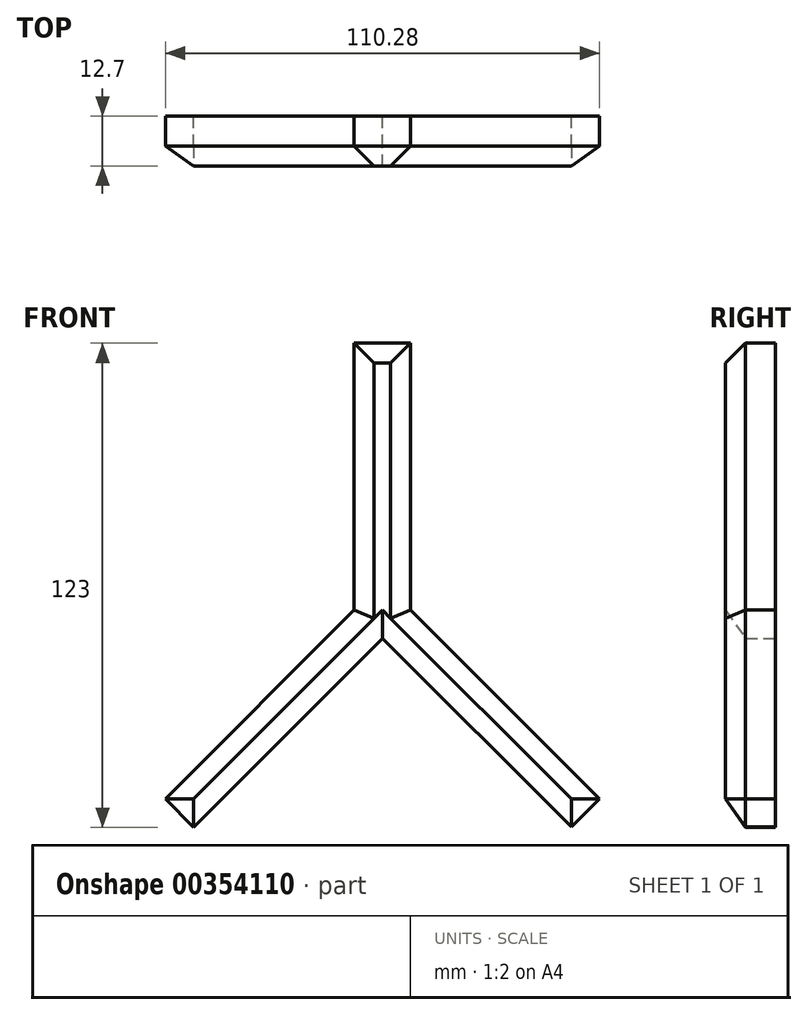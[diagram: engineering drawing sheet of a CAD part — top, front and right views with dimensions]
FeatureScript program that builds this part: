
annotation { "Feature Type Name" : "Feature", "Feature Type Description" : "" }
export const myFeature = defineFeature(function(context is Context, id is Id, definition is map)
    precondition{}
    {
        {
            var Q0;
            Q0=qCreatedBy(makeId("Front.planeOp"),FACE);
            var sketch = newSketch(context, id + "F0", { "sketchPlane" : qUnion([Q0])});
            skLineSegment(sketch, "E0", {"start": v(-7.19, 7.18) * mm, "end": v(-7.19, 75) * mm});
            skLineSegment(sketch, "E1", {"start": v(-7.19, 75) * mm, "end": v(7.18, 75) * mm});
            skLineSegment(sketch, "E2", {"start": v(7.18, 75) * mm, "end": v(7.18, 7.18) * mm});
            skLineSegment(sketch, "E3", {"start": v(0, 0) * mm, "end": v(-47.9, -48) * mm});
            skLineSegment(sketch, "E4", {"start": v(-47.9, -48) * mm, "end": v(-55.1, -40.82) * mm});
            skLineSegment(sketch, "E5", {"start": v(-55.1, -40.82) * mm, "end": v(-7.19, 7.18) * mm});
            skLineSegment(sketch, "E6", {"start": v(0, 0) * mm, "end": v(48, -47.9) * mm});
            skLineSegment(sketch, "E7", {"start": v(48, -47.9) * mm, "end": v(55.18, -40.72) * mm});
            skLineSegment(sketch, "E8", {"start": v(7.18, 7.18) * mm, "end": v(55.18, -40.72) * mm});
            skSolve(sketch);
        }
        {
            var Q0;
            Q0 = qSketchRegion(id + "F0", true);
            extrude(context, id + "F1", {"entities" : qUnion([Q0]), "depth" : 12.7 * mm});
        }
        {
            var Q0;
            Q0=makeQuery(id+"F1.opExtrude","CAP_FACE",FACE,{"disambiguationData":[OSD([sQuery(id+"F0.wireOp",EDGE,"E0"),sQuery(id+"F0.wireOp",EDGE,"E1"),sQuery(id+"F0.wireOp",EDGE,"E2"),sQuery(id+"F0.wireOp",EDGE,"E3"),sQuery(id+"F0.wireOp",EDGE,"E4"),sQuery(id+"F0.wireOp",EDGE,"E5"),sQuery(id+"F0.wireOp",EDGE,"E6"),sQuery(id+"F0.wireOp",EDGE,"E7"),sQuery(id+"F0.wireOp",EDGE,"E8")])],"isStart":false});
            chamfer(context, id + "F2", {"entities" : qUnion([Q0]), "width" : 5.08 * mm, "tangentPropagation" : true});
        }
    });
